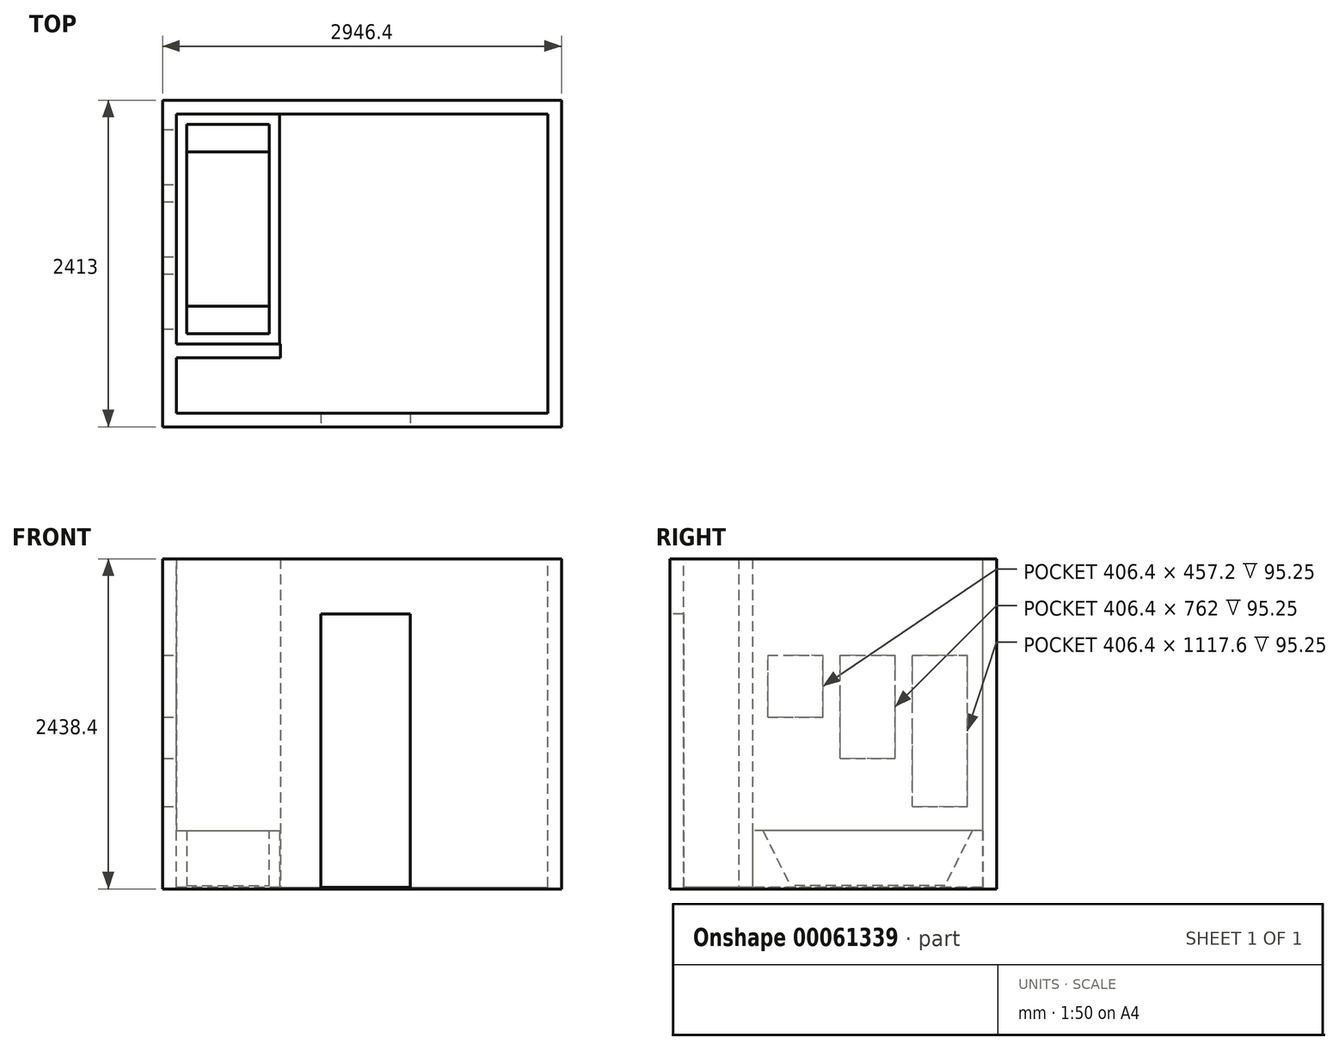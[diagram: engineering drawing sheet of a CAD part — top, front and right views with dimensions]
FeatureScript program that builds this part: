
annotation { "Feature Type Name" : "Feature", "Feature Type Description" : "" }
export const myFeature = defineFeature(function(context is Context, id is Id, definition is map)
    precondition{}
    {
        {
            var Q0;
            Q0=qCreatedBy(makeId("Top.planeOp"),FACE);
            var sketch = newSketch(context, id + "F0", { "sketchPlane" : qUnion([Q0])});
            skLineSegment(sketch, "E0.bottom", {"start": v(-1473.2, 1206.5) * mm, "end": v(1473.2, 1206.5) * mm});
            skLineSegment(sketch, "E0.top", {"start": v(-1473.2, -1206.5) * mm, "end": v(1473.2, -1206.5) * mm});
            skLineSegment(sketch, "E0.left", {"start": v(-1473.2, 1206.5) * mm, "end": v(-1473.2, -1206.5) * mm});
            skLineSegment(sketch, "E0.right", {"start": v(1473.2, 1206.5) * mm, "end": v(1473.2, -1206.5) * mm});
            skSolve(sketch);
        }
        {
            var Q0;
            Q0=makeQuery(id+"F0.imprint","IMPRINT",FACE,{"disambiguationData":[TD([[makeQuery(id+"F0.imprint","IMPRINT",EDGE,{"derivedFrom":sQuery(id+"F0.wireOp",EDGE,"E0.bottom")}),-1.0]])]});
            extrude(context, id + "F1", {"entities" : qUnion([Q0]), "depth" : 2438.4 * mm});
        }
        {
            var Q0;
            Q0=makeQuery(id+"F1.opExtrude","CAP_FACE",FACE,{"disambiguationData":[OSD([sQuery(id+"F0.wireOp",EDGE,"E0.bottom"),sQuery(id+"F0.wireOp",EDGE,"E0.top"),sQuery(id+"F0.wireOp",EDGE,"E0.left"),sQuery(id+"F0.wireOp",EDGE,"E0.right")])],"isStart":false});
            var sketch = newSketch(context, id + "F2", { "sketchPlane" : qUnion([Q0])});
            skLineSegment(sketch, "E1.bottom", {"start": v(-1371.6, 1104.9) * mm, "end": v(1371.6, 1104.9) * mm});
            skLineSegment(sketch, "E1.top", {"start": v(-1371.6, -1104.9) * mm, "end": v(1371.6, -1104.9) * mm});
            skLineSegment(sketch, "E1.left", {"start": v(-1371.6, 1104.9) * mm, "end": v(-1371.6, -1104.9) * mm});
            skLineSegment(sketch, "E1.right", {"start": v(1371.6, 1104.9) * mm, "end": v(1371.6, -1104.9) * mm});
            skSolve(sketch);
        }
        {
            var Q0;
            Q0 = qSketchRegion(id + "F2", true);
            extrude(context, id + "F3", {"entities" : qUnion([Q0]), "operationType" : NewBodyOperationType.REMOVE, "oppositeDirection" : true, "depth" : 2425.7 * mm});
        }
        {
            var Q0;
            Q0=qCreatedBy(makeId("Top.planeOp"),FACE);
            var sketch = newSketch(context, id + "F4", { "sketchPlane" : qUnion([Q0])});
            skLineSegment(sketch, "E2.bottom", {"start": v(-1371.6, 1104.9) * mm, "end": v(-609.6, 1104.9) * mm});
            skLineSegment(sketch, "E2.top", {"start": v(-1371.6, -595.12) * mm, "end": v(-609.6, -595.12) * mm});
            skLineSegment(sketch, "E2.left", {"start": v(-1371.6, 1104.9) * mm, "end": v(-1371.6, -595.12) * mm});
            skLineSegment(sketch, "E2.right", {"start": v(-609.6, 1104.9) * mm, "end": v(-609.6, -595.12) * mm});
            skSolve(sketch);
        }
        {
            var Q0;
            Q0 = qSketchRegion(id + "F4", true);
            extrude(context, id + "F5", {"entities" : qUnion([Q0]), "depth" : 431.8 * mm});
        }
        {
            var Q0;
            Q0=makeQuery(id+"F5.opExtrude","CAP_FACE",FACE,{"disambiguationData":[OSD([sQuery(id+"F4.wireOp",EDGE,"E2.bottom"),sQuery(id+"F4.wireOp",EDGE,"E2.top"),sQuery(id+"F4.wireOp",EDGE,"E2.left"),sQuery(id+"F4.wireOp",EDGE,"E2.right")])],"isStart":false});
            var sketch = newSketch(context, id + "F6", { "sketchPlane" : qUnion([Q0])});
            skLineSegment(sketch, "E3.bottom", {"start": v(-1295.4, 1028.7) * mm, "end": v(-685.8, 1028.7) * mm});
            skLineSegment(sketch, "E3.top", {"start": v(-1295.4, -518.92) * mm, "end": v(-685.8, -518.92) * mm});
            skLineSegment(sketch, "E3.left", {"start": v(-1295.4, 1028.7) * mm, "end": v(-1295.4, -518.92) * mm});
            skLineSegment(sketch, "E3.right", {"start": v(-685.8, 1028.7) * mm, "end": v(-685.8, -518.92) * mm});
            skSolve(sketch);
        }
        {
            var Q0;
            Q0 = qSketchRegion(id + "F6", true);
            extrude(context, id + "F7", {"entities" : qUnion([Q0]), "operationType" : NewBodyOperationType.REMOVE, "oppositeDirection" : true, "depth" : 406.4 * mm});
        }
        {
            var Q0;
            Q0=makeQuery(id+"F7.boolean.opBoolean","COPY",EDGE,{"derivedFrom":makeQuery(id+"F7.opExtrude","CAP_EDGE",EDGE,{"disambiguationData":[OSD([sQuery(id+"F6.wireOp",EDGE,"E3.bottom")])],"isStart":false})});
            var Q1;
            Q1=makeQuery(id+"F7.boolean.opBoolean","COPY",EDGE,{"derivedFrom":makeQuery(id+"F7.opExtrude","CAP_EDGE",EDGE,{"disambiguationData":[OSD([sQuery(id+"F6.wireOp",EDGE,"E3.top")])],"isStart":false})});
            chamfer(context, id + "F8", {"entities" : qUnion([Q0, Q1]), "chamferType" : ChamferType.TWO_OFFSETS, "width1" : 406.4 * mm, "oppositeDirection" : false, "width2" : 203.2 * mm, "tangentPropagation" : true});
        }
        {
            var Q0;
            Q0=qCreatedBy(makeId("Top.planeOp"),FACE);
            var sketch = newSketch(context, id + "F9", { "sketchPlane" : qUnion([Q0])});
            skLineSegment(sketch, "E4.bottom", {"start": v(-1371.6, -696.72) * mm, "end": v(-603.25, -696.72) * mm});
            skLineSegment(sketch, "E4.top", {"start": v(-1371.6, -595.12) * mm, "end": v(-603.25, -595.12) * mm});
            skLineSegment(sketch, "E4.left", {"start": v(-1371.6, -696.72) * mm, "end": v(-1371.6, -595.12) * mm});
            skLineSegment(sketch, "E4.right", {"start": v(-603.25, -696.72) * mm, "end": v(-603.25, -595.12) * mm});
            skSolve(sketch);
        }
        {
            var Q0;
            Q0 = qSketchRegion(id + "F9", true);
            extrude(context, id + "F10", {"entities" : qUnion([Q0]), "operationType" : NewBodyOperationType.ADD, "depth" : 2438.4 * mm});
        }
        {
            var Q0;
            Q0=makeQuery(id+"F1.opExtrude","SWEPT_FACE",FACE,{"disambiguationData":[OSD([sQuery(id+"F0.wireOp",EDGE,"E0.top")])]});
            var sketch = newSketch(context, id + "F11", { "sketchPlane" : qUnion([Q0])});
            skLineSegment(sketch, "E5.bottom", {"start": v(-304.8, 2032) * mm, "end": v(355.6, 2032) * mm});
            skLineSegment(sketch, "E5.top", {"start": v(-304.8, 0) * mm, "end": v(355.6, 0) * mm});
            skLineSegment(sketch, "E5.left", {"start": v(-304.8, 2032) * mm, "end": v(-304.8, 0) * mm});
            skLineSegment(sketch, "E5.right", {"start": v(355.6, 2032) * mm, "end": v(355.6, 0) * mm});
            skSolve(sketch);
        }
        {
            var Q0;
            Q0 = qSketchRegion(id + "F11", true);
            extrude(context, id + "F12", {"entities" : qUnion([Q0]), "operationType" : NewBodyOperationType.REMOVE, "oppositeDirection" : true, "depth" : 101.6 * mm});
        }
        {
            var Q0;
            {var subQ0=sQuery(id+"F2.wireOp",EDGE,"E1.left");var subQ1=sQuery(id+"F2.wireOp",EDGE,"E1.bottom");Q0=makeQuery(id+"F10.boolean.opBoolean","SPLIT",FACE,{"disambiguationData":[TD([makeQuery(id+"F3.boolean.opBoolean","COPY",FACE,{"derivedFrom":makeQuery(id+"F3.opExtrude","SWEPT_FACE",FACE,{"disambiguationData":[OSD([subQ1])]})})])],"derivedFrom":makeQuery(id+"F3.boolean.opBoolean","COPY",FACE,{"derivedFrom":makeQuery(id+"F3.opExtrude","SWEPT_FACE",FACE,{"disambiguationData":[OSD([subQ0])]})})});}
            var sketch = newSketch(context, id + "F13", { "sketchPlane" : qUnion([Q0])});
            skLineSegment(sketch, "E6.bottom", {"start": v(584.2, 609.6) * mm, "end": v(990.6, 609.6) * mm});
            skLineSegment(sketch, "E6.top", {"start": v(584.2, 1727.2) * mm, "end": v(990.6, 1727.2) * mm});
            skLineSegment(sketch, "E6.left", {"start": v(584.2, 609.6) * mm, "end": v(584.2, 1727.2) * mm});
            skLineSegment(sketch, "E6.right", {"start": v(990.6, 609.6) * mm, "end": v(990.6, 1727.2) * mm});
            skLineSegment(sketch, "E7.bottom", {"start": v(50.8, 965.2) * mm, "end": v(457.2, 965.2) * mm});
            skLineSegment(sketch, "E7.top", {"start": v(50.8, 1727.2) * mm, "end": v(457.2, 1727.2) * mm});
            skLineSegment(sketch, "E7.left", {"start": v(50.8, 965.2) * mm, "end": v(50.8, 1727.2) * mm});
            skLineSegment(sketch, "E7.right", {"start": v(457.2, 965.2) * mm, "end": v(457.2, 1727.2) * mm});
            skLineSegment(sketch, "E8.bottom", {"start": v(-482.6, 1270) * mm, "end": v(-76.2, 1270) * mm});
            skLineSegment(sketch, "E8.top", {"start": v(-482.6, 1727.2) * mm, "end": v(-76.2, 1727.2) * mm});
            skLineSegment(sketch, "E8.left", {"start": v(-482.6, 1270) * mm, "end": v(-482.6, 1727.2) * mm});
            skLineSegment(sketch, "E8.right", {"start": v(-76.2, 1270) * mm, "end": v(-76.2, 1727.2) * mm});
            skSolve(sketch);
        }
        {
            var Q0;
            Q0 = qSketchRegion(id + "F13", true);
            extrude(context, id + "F14", {"entities" : qUnion([Q0]), "operationType" : NewBodyOperationType.REMOVE, "oppositeDirection" : true, "depth" : 95.25 * mm});
        }
    });
